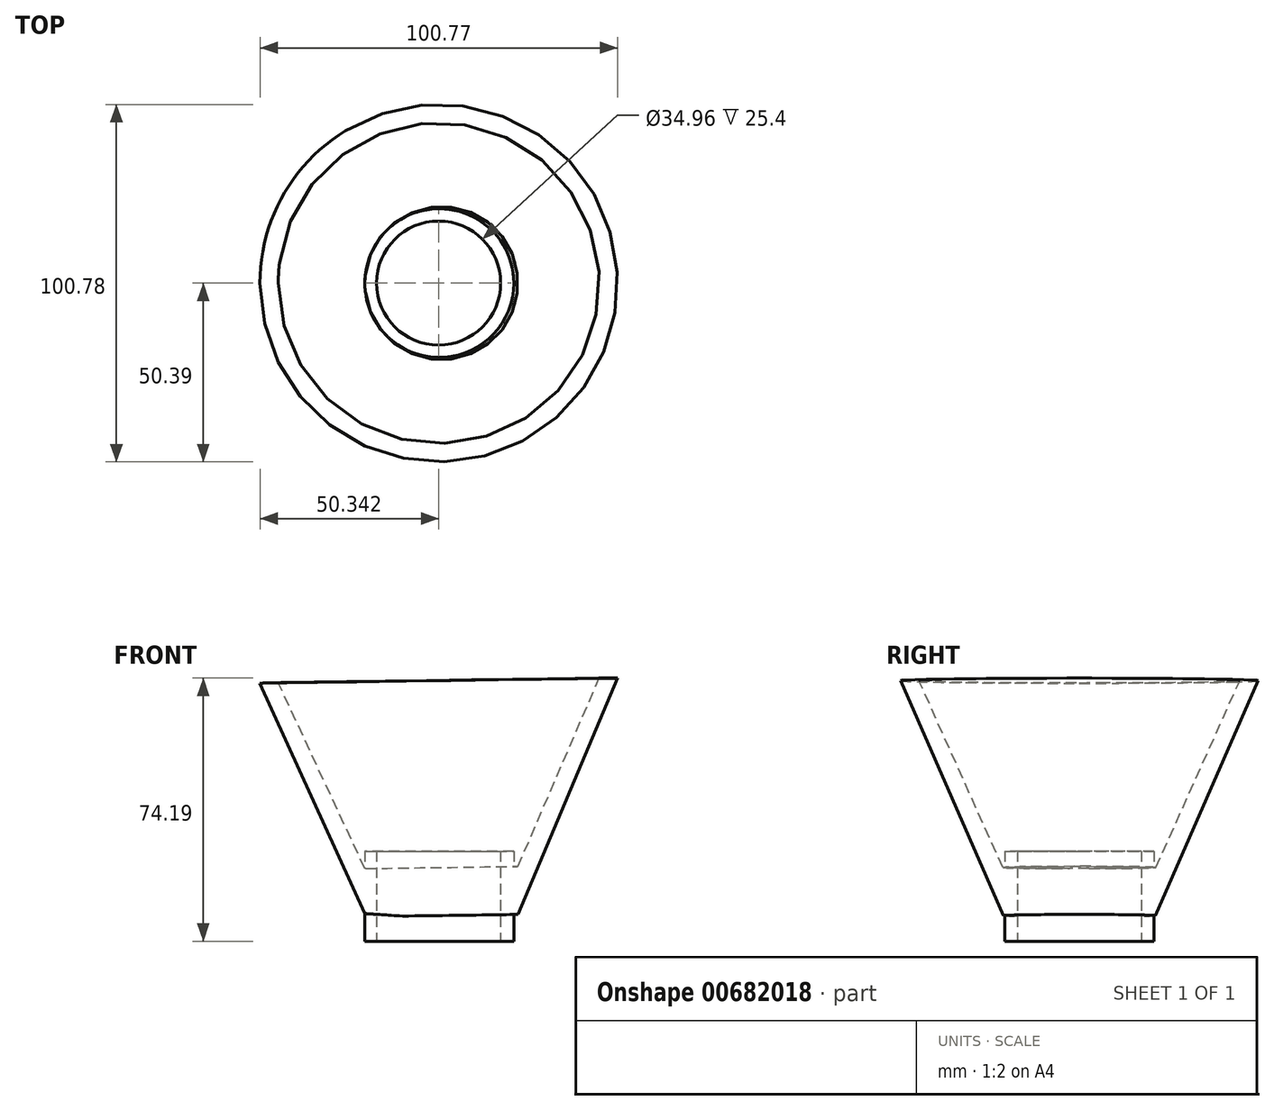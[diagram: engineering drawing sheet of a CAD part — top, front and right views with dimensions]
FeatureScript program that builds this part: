
annotation { "Feature Type Name" : "Feature", "Feature Type Description" : "" }
export const myFeature = defineFeature(function(context is Context, id is Id, definition is map)
    precondition{}
    {
        {
            var Q0;
            Q0=qCreatedBy(makeId("Front.planeOp"),FACE);
            var sketch = newSketch(context, id + "F0", { "sketchPlane" : qUnion([Q0])});
            skLineSegment(sketch, "E0", {"start": v(-54.52, 21.1) * mm, "end": v(-32.94, 21.1) * mm});
            skLineSegment(sketch, "E1", {"start": v(-32.94, 21.1) * mm, "end": v(-10.03, 74.19) * mm});
            skLineSegment(sketch, "E2", {"start": v(-10.03, 74.19) * mm, "end": v(-4.87, 74.19) * mm});
            skLineSegment(sketch, "E3", {"start": v(-4.87, 74.19) * mm, "end": v(-32.94, 7.54) * mm});
            skLineSegment(sketch, "E4", {"start": v(-32.94, 7.54) * mm, "end": v(-54.33, 7.54) * mm});
            skLineSegment(sketch, "E5", {"start": v(-54.33, 7.54) * mm, "end": v(-54.52, 21.1) * mm});
            skSolve(sketch);
        }
        {
            var Q0;
            Q0=makeQuery(id+"F0.imprint","IMPRINT",FACE,{"disambiguationData":[TD([[makeQuery(id+"F0.imprint","IMPRINT",EDGE,{"derivedFrom":sQuery(id+"F0.wireOp",EDGE,"E0")}),-1.0]])]});
            var Q1;
            Q1=sQuery(id+"F0.wireOp",EDGE,"E5");
            revolve(context, id + "F1", {"entities" : qUnion([Q0]), "axis" : qUnion([Q1]), "revolveType" : RevolveType.FULL});
        }
        {
            var Q0;
            Q0=qCreatedBy(makeId("Top.planeOp"),FACE);
            var sketch = newSketch(context, id + "F2", { "sketchPlane" : qUnion([Q0])});
            skCircle(sketch, "E6", {"center": v(-55.1, 0) * mm, "radius": 20.98 * mm});
            skSolve(sketch);
        }
        {
            var Q0;
            Q0 = qSketchRegion(id + "F2", true);
            extrude(context, id + "F3", {"entities" : qUnion([Q0]), "operationType" : NewBodyOperationType.ADD, "depth" : 25.4 * mm, "offsetDistance" : 25.4 * mm});
        }
        {
            var Q0;
            Q0=makeQuery(id+"F3.opExtrude","CAP_FACE",FACE,{"disambiguationData":[OSD([sQuery(id+"F2.wireOp",EDGE,"E6")])],"isStart":true});
            var sketch = newSketch(context, id + "F4", { "sketchPlane" : qUnion([Q0])});
            skSolve(sketch);
        }
        {
            var Q0;
            Q0=makeQuery(id+"F4.imprint","IMPRINT",FACE,{"disambiguationData":[TD([[makeQuery(id+"F4.imprint","IMPRINT",EDGE,{"derivedFrom":makeQuery(id+"F3.opExtrude","CAP_EDGE",EDGE,{"disambiguationData":[OSD([sQuery(id+"F2.wireOp",EDGE,"E6")])],"isStart":true})}),-1.0]])]});
            var sketch = newSketch(context, id + "F5", { "sketchPlane" : qUnion([Q0])});
            skCircle(sketch, "E7", {"center": v(-55.3, 0) * mm, "radius": 17.48 * mm});
            skSolve(sketch);
        }
        {
            var Q0;
            Q0 = qSketchRegion(id + "F5", true);
            extrude(context, id + "F6", {"entities" : qUnion([Q0]), "operationType" : NewBodyOperationType.REMOVE, "oppositeDirection" : true, "depth" : 25.4 * mm, "offsetDistance" : 25.4 * mm});
        }
    });
